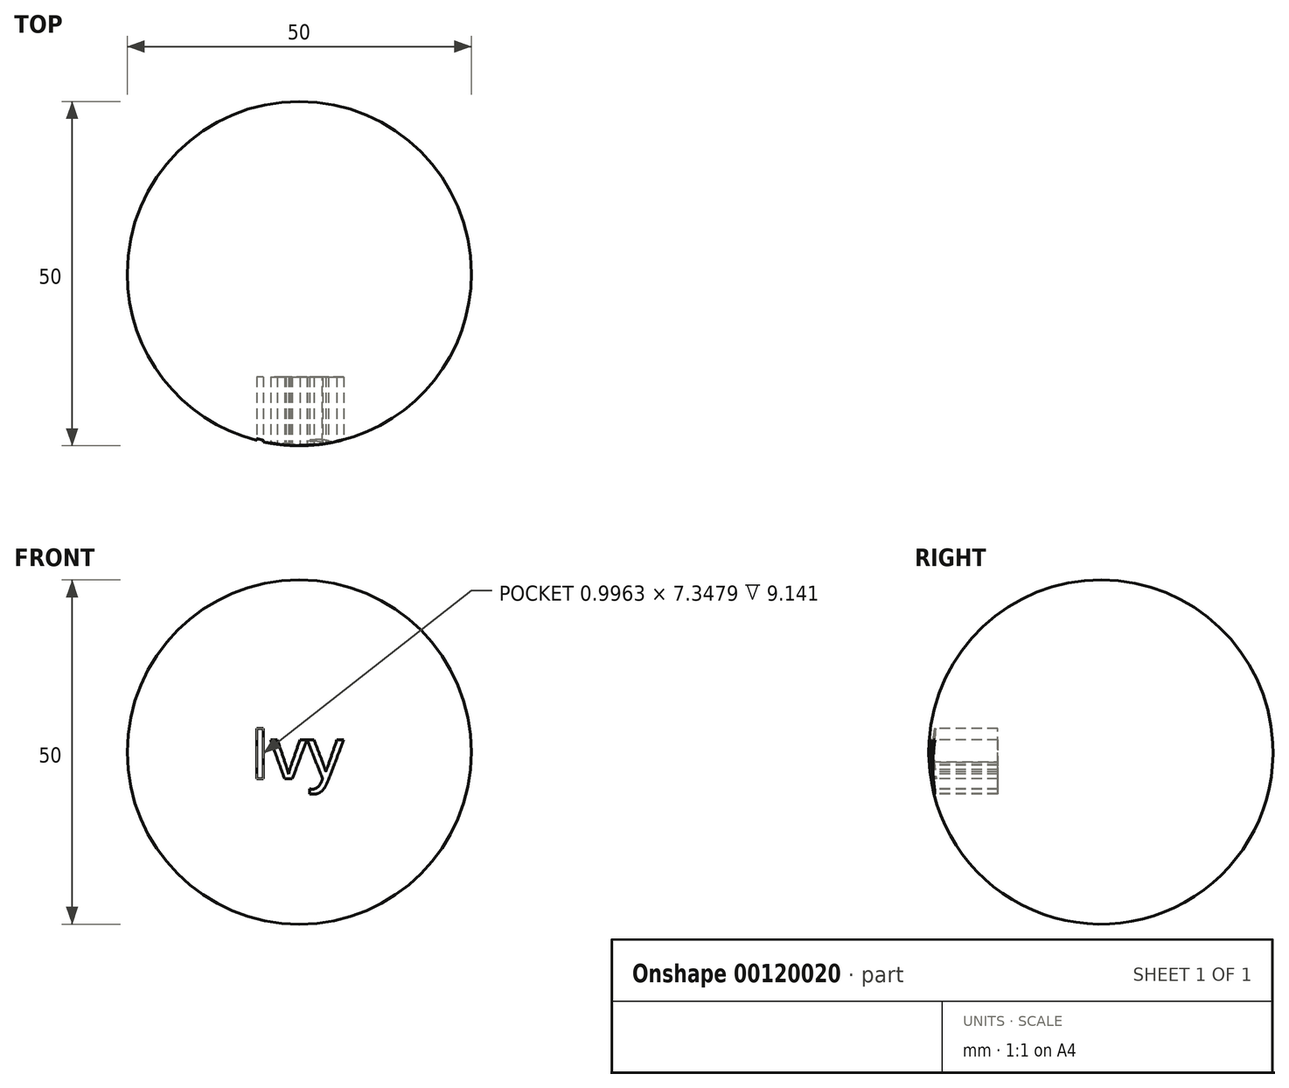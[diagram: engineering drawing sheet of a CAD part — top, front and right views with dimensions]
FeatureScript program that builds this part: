
annotation { "Feature Type Name" : "Feature", "Feature Type Description" : "" }
export const myFeature = defineFeature(function(context is Context, id is Id, definition is map)
    precondition{}
    {
        {
            var Q0;
            Q0=qCreatedBy(makeId("Top.planeOp"),FACE);
            var sketch = newSketch(context, id + "F0", { "sketchPlane" : qUnion([Q0])});
            skCircle(sketch, "E0", {"center": v(0, 0) * mm, "radius": 25 * mm});
            skLineSegment(sketch, "E1", {"start": v(25, 0) * mm, "end": v(-25, 0) * mm});
            skSolve(sketch);
        }
        {
            var Q0;
            {var subQ0=sQuery(id+"F0.wireOp",EDGE,"E1");Q0=makeQuery(id+"F0.imprint","IMPRINT",FACE,{"disambiguationData":[TD([[makeQuery(id+"F0.imprint","IMPRINT",EDGE,{"derivedFrom":subQ0}),-1.0]])]});}
            var Q1;
            Q1=sQuery(id+"F0.wireOp",EDGE,"E1");
            revolve(context, id + "F1", {"entities" : qUnion([Q0]), "axis" : qUnion([Q1]), "revolveType" : RevolveType.FULL});
        }
        {
            var Q0;
            Q0=qCreatedBy(makeId("Front.planeOp"),FACE);
            cPlane(context, id + "F2", {"entities" : qUnion([Q0]), "cplaneType" : CPlaneType.OFFSET, "offset" : 25 * mm, "width" : 150 * mm, "height" : 150 * mm});
        }
        {
            var Q0;
            Q0=qCreatedBy(id+"F2.planeOp",FACE);
            var sketch = newSketch(context, id + "F3", { "sketchPlane" : qUnion([Q0])});
            skText(sketch, "E2", { "text": "Ivy", "fontName": "Arimo-Regular.ttf"});
            const initialGuessF3  = {"E2": [-0.00718, -0.0039, 1, 0, 0.00769]};
            skSetInitialGuess(sketch, initialGuessF3);
            skSolve(sketch);
        }
        {
            var Q0;
            Q0=makeQuery(id+"F3.imprint","IMPRINT",FACE,{"disambiguationData":[TD([[makeQuery(id+"F3.imprint","IMPRINT",EDGE,{"derivedFrom":sQuery(id+"F3.wireOp",EDGE,"E2.sketch_text.stroke-4")}),-1.0]])]});
            extrude(context, id + "F4", {"entities" : qUnion([Q0]), "operationType" : NewBodyOperationType.REMOVE, "oppositeDirection" : true, "depth" : 10 * mm});
        }
        {
            var Q0;
            Q0=makeQuery(id+"F3.imprint","IMPRINT",FACE,{"disambiguationData":[TD([[makeQuery(id+"F3.imprint","IMPRINT",EDGE,{"derivedFrom":sQuery(id+"F3.wireOp",EDGE,"E2.sketch_text.stroke-0")}),-1.0]])]});
            extrude(context, id + "F5", {"entities" : qUnion([Q0]), "operationType" : NewBodyOperationType.REMOVE, "oppositeDirection" : true, "depth" : 10 * mm});
        }
        {
            var Q0;
            Q0=makeQuery(id+"F3.imprint","IMPRINT",FACE,{"disambiguationData":[TD([[makeQuery(id+"F3.imprint","IMPRINT",EDGE,{"derivedFrom":sQuery(id+"F3.wireOp",EDGE,"E2.sketch_text.stroke-14")}),-1.0]])]});
            extrude(context, id + "F6", {"entities" : qUnion([Q0]), "operationType" : NewBodyOperationType.REMOVE, "oppositeDirection" : true, "depth" : 10 * mm});
        }
    });
